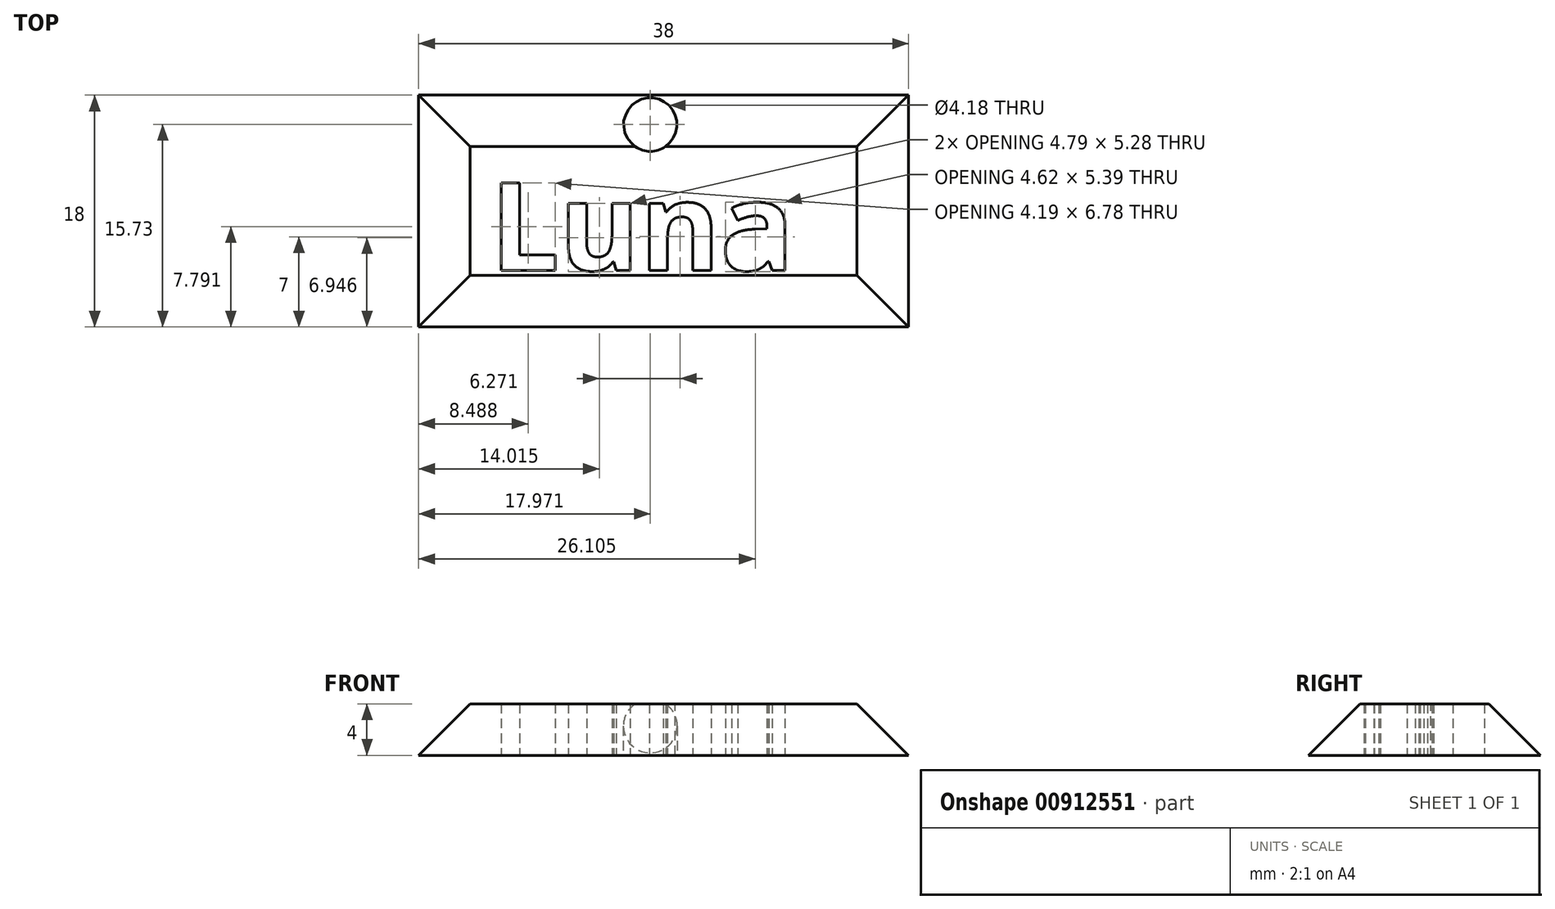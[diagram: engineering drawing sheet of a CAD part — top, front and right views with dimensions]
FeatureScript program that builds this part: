
annotation { "Feature Type Name" : "Feature", "Feature Type Description" : "" }
export const myFeature = defineFeature(function(context is Context, id is Id, definition is map)
    precondition{}
    {
        {
            var Q0;
            Q0=qCreatedBy(makeId("Top.planeOp"),FACE);
            var sketch = newSketch(context, id + "F0", { "sketchPlane" : qUnion([Q0])});
            skLineSegment(sketch, "E0.bottom", {"start": v(0, 0) * mm, "end": v(40, 0) * mm});
            skLineSegment(sketch, "E0.top", {"start": v(0, 20) * mm, "end": v(40, 20) * mm});
            skLineSegment(sketch, "E0.left", {"start": v(0, 0) * mm, "end": v(0, 20) * mm});
            skLineSegment(sketch, "E0.right", {"start": v(40, 0) * mm, "end": v(40, 20) * mm});
            skText(sketch, "E1", { "text": "Luna", "fontName": "OpenSans-Bold.ttf"});
            skCircle(sketch, "E2", {"center": v(18.97, 16.73) * mm, "radius": 2.09 * mm});
            const initialGuessF0  = {"E1": [0.00654, 0.0054, 1, 0, 0.00684]};
            skSetInitialGuess(sketch, initialGuessF0);
            skSolve(sketch);
        }
        {
            var Q0;
            Q0=makeQuery(id+"F0.imprint","IMPRINT",FACE,{"disambiguationData":[TD([[makeQuery(id+"F0.imprint","IMPRINT",EDGE,{"derivedFrom":sQuery(id+"F0.wireOp",EDGE,"E0.bottom")}),1.0]])]});
            extrude(context, id + "F1", {"entities" : qUnion([Q0]), "depth" : 4 * mm, "offsetDistance" : 25 * mm});
        }
        {
            var Q0;
            Q0=makeQuery(id+"F1.opExtrude","CAP_EDGE",EDGE,{"disambiguationData":[OSD([sQuery(id+"F0.wireOp",EDGE,"E0.top")])],"isStart":false});
            var Q1;
            Q1=makeQuery(id+"F1.opExtrude","CAP_EDGE",EDGE,{"disambiguationData":[OSD([sQuery(id+"F0.wireOp",EDGE,"E0.left")])],"isStart":false});
            var Q2;
            Q2=makeQuery(id+"F1.opExtrude","CAP_EDGE",EDGE,{"disambiguationData":[OSD([sQuery(id+"F0.wireOp",EDGE,"E0.bottom")])],"isStart":false});
            var Q3;
            Q3=makeQuery(id+"F1.opExtrude","CAP_EDGE",EDGE,{"disambiguationData":[OSD([sQuery(id+"F0.wireOp",EDGE,"E0.right")])],"isStart":false});
            chamfer(context, id + "F2", {"entities" : qUnion([Q0, Q1, Q2, Q3]), "width" : 5 * mm, "tangentPropagation" : true});
        }
    });
